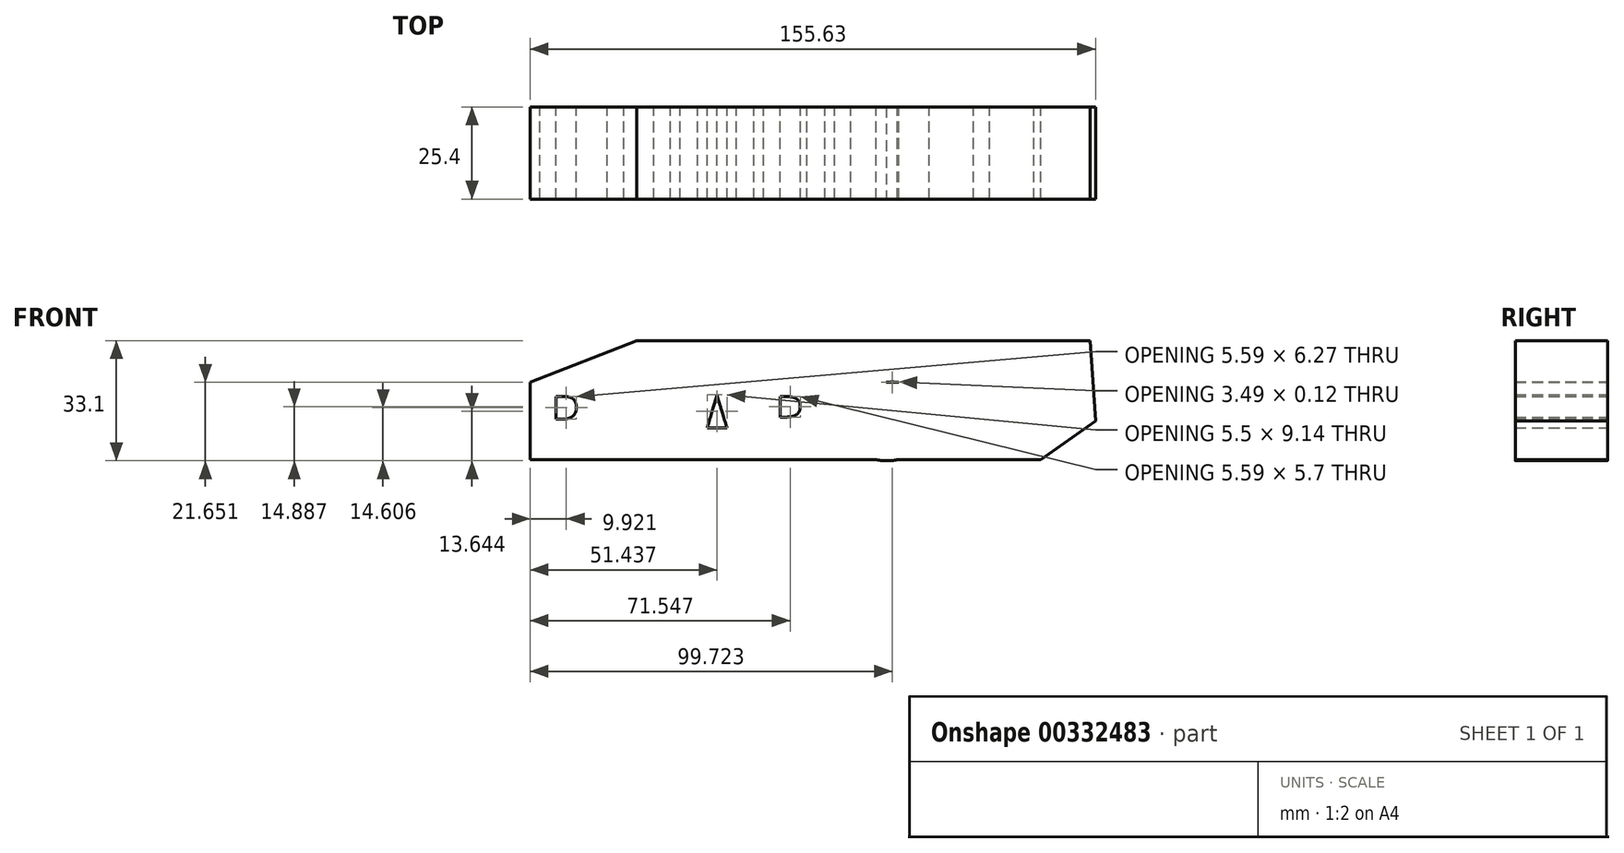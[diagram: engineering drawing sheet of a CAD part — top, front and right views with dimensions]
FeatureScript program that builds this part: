
annotation { "Feature Type Name" : "Feature", "Feature Type Description" : "" }
export const myFeature = defineFeature(function(context is Context, id is Id, definition is map)
    precondition{}
    {
        {
            var Q0;
            Q0=qCreatedBy(makeId("Front.planeOp"),FACE);
            var sketch = newSketch(context, id + "F0", { "sketchPlane" : qUnion([Q0])});
            skPoint(sketch, "E0.0", {"position": v(0, 0) * mm});
            skText(sketch, "E1", { "text": "PHARISEE", "fontName": "OpenSans-Bold.ttf"});
            skLineSegment(sketch, "E2", {"start": v(-38, 18.13) * mm, "end": v(-8.7, 29.64) * mm});
            skLineSegment(sketch, "E3", {"start": v(-8.7, 29.64) * mm, "end": v(84.26, 29.64) * mm});
            skLineSegment(sketch, "E4", {"start": v(84.26, 29.64) * mm, "end": v(116.2, 29.64) * mm});
            skLineSegment(sketch, "E5", {"start": v(116.2, 29.64) * mm, "end": v(102.54, 18.13) * mm});
            skLineSegment(sketch, "E6", {"start": v(102.54, -3.17) * mm, "end": v(117.64, 7.48) * mm});
            skPoint(sketch, "E6.endSnap0", {"position": v(102.54, 7.48) * mm});
            skLineSegment(sketch, "E7", {"start": v(117.64, 7.48) * mm, "end": v(116.2, 29.64) * mm});
            skLineSegment(sketch, "E8", {"start": v(-38, -3.17) * mm, "end": v(-38, 18.13) * mm});
            skLineSegment(sketch, "E9", {"start": v(-38, -3.17) * mm, "end": v(102.54, -3.17) * mm});
            skLineSegment(sketch, "E10", {"start": v(102.54, 18.13) * mm, "end": v(102.54, -3.17) * mm});
            skLineSegment(sketch, "E11", {"start": v(102.54, 18.13) * mm, "end": v(-38, 18.13) * mm});
            skLineSegment(sketch, "E12", {"start": v(-19.28, 18.13) * mm, "end": v(-19.28, -3.17) * mm});
            skLineSegment(sketch, "E13", {"start": v(2.02, -3.17) * mm, "end": v(2.02, 18.13) * mm});
            skLineSegment(sketch, "E14", {"start": v(24.75, -3.17) * mm, "end": v(24.75, 18.13) * mm});
            skLineSegment(sketch, "E15", {"start": v(44.32, -3.17) * mm, "end": v(44.32, 18.13) * mm});
            skLineSegment(sketch, "E16", {"start": v(52.1, -3.17) * mm, "end": v(52.1, 18.13) * mm});
            skLineSegment(sketch, "E17", {"start": v(69.94, -3.17) * mm, "end": v(69.94, 18.13) * mm});
            skLineSegment(sketch, "E18", {"start": v(86.34, -3.17) * mm, "end": v(86.34, 18.13) * mm});
            const initialGuessF0  = {"E1": [-0.038, -0.00317, 1, 0, 0.0213]};
            skSetInitialGuess(sketch, initialGuessF0);
            skSolve(sketch);
        }
        {
            var Q0;
            Q0 = qSketchRegion(id + "F0", true);
            extrude(context, id + "F1", {"entities" : qUnion([Q0]), "depth" : 25.4 * mm});
        }
    });
